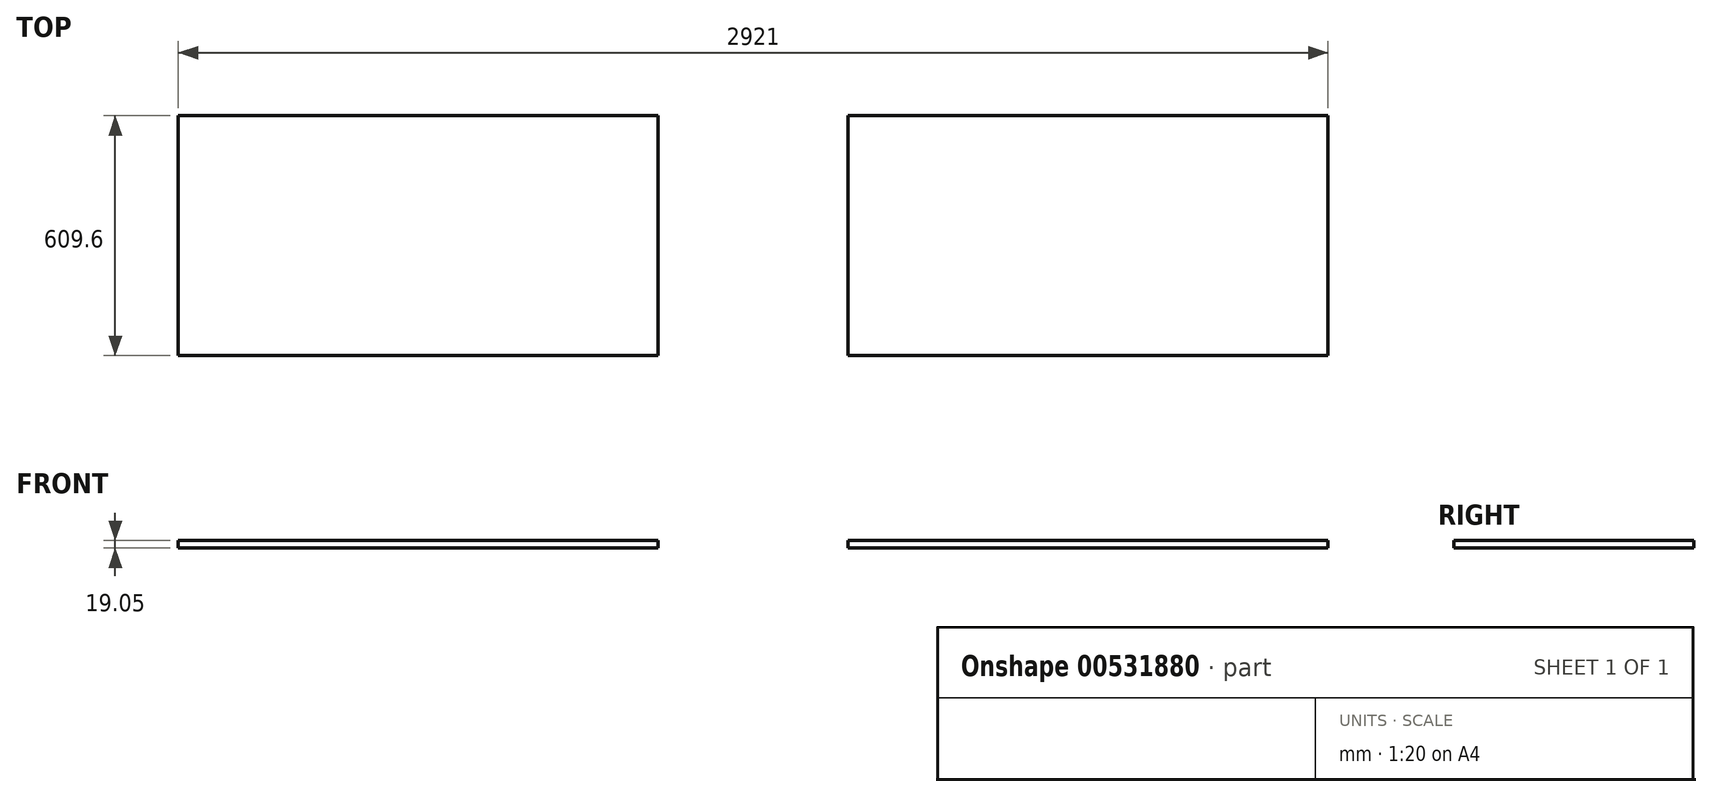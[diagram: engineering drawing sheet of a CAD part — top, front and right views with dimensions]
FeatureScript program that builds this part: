
annotation { "Feature Type Name" : "Feature", "Feature Type Description" : "" }
export const myFeature = defineFeature(function(context is Context, id is Id, definition is map)
    precondition{}
    {
        {
            var Q0;
            Q0=qCreatedBy(makeId("Top.planeOp"),FACE);
            var sketch = newSketch(context, id + "F0", { "sketchPlane" : qUnion([Q0])});
            skLineSegment(sketch, "E0.bottom", {"start": v(0, 0) * mm, "end": v(1219.2, 0) * mm});
            skLineSegment(sketch, "E0.top", {"start": v(0, 609.6) * mm, "end": v(1219.2, 609.6) * mm});
            skLineSegment(sketch, "E0.left", {"start": v(0, 0) * mm, "end": v(0, 609.6) * mm});
            skLineSegment(sketch, "E0.right", {"start": v(1219.2, 0) * mm, "end": v(1219.2, 609.6) * mm});
            skSolve(sketch);
        }
        {
            var Q0;
            Q0 = qSketchRegion(id + "F0", true);
            extrude(context, id + "F1", {"entities" : qUnion([Q0]), "depth" : 19.05 * mm, "offsetDistance" : 25.4 * mm});
        }
        {
            var Q0;
            Q0=makeQuery(id+"F1.opExtrude","CAP_FACE",FACE,{"disambiguationData":[OSD([sQuery(id+"F0.wireOp",EDGE,"E0.bottom"),sQuery(id+"F0.wireOp",EDGE,"E0.top"),sQuery(id+"F0.wireOp",EDGE,"E0.left"),sQuery(id+"F0.wireOp",EDGE,"E0.right")])],"isStart":false});
            var sketch = newSketch(context, id + "F2", { "sketchPlane" : qUnion([Q0])});
            skLineSegment(sketch, "E1.bottom", {"start": v(-1701.8, 609.6) * mm, "end": v(-482.6, 609.6) * mm});
            skLineSegment(sketch, "E1.top", {"start": v(-1701.8, 0) * mm, "end": v(-482.6, 0) * mm});
            skLineSegment(sketch, "E1.left", {"start": v(-1701.8, 609.6) * mm, "end": v(-1701.8, 0) * mm});
            skLineSegment(sketch, "E1.right", {"start": v(-482.6, 609.6) * mm, "end": v(-482.6, 0) * mm});
            skSolve(sketch);
        }
        {
            var Q0;
            Q0=makeQuery(id+"F2.imprint","IMPRINT",FACE,{"disambiguationData":[TD([[makeQuery(id+"F2.imprint","IMPRINT",EDGE,{"derivedFrom":sQuery(id+"F2.wireOp",EDGE,"E1.bottom")}),-1.0]])]});
            var Q1;
            Q1=makeQuery(id+"F1.opExtrude","CAP_FACE",FACE,{"disambiguationData":[OSD([sQuery(id+"F0.wireOp",EDGE,"E0.bottom"),sQuery(id+"F0.wireOp",EDGE,"E0.top"),sQuery(id+"F0.wireOp",EDGE,"E0.left"),sQuery(id+"F0.wireOp",EDGE,"E0.right")])],"isStart":false});
            var Q2;
            Q2=makeQuery(id+"F1.opExtrude","SWEPT_BODY",BODY,{"disambiguationData":[OSD([sQuery(id+"F0.wireOp",EDGE,"E0.bottom"),sQuery(id+"F0.wireOp",EDGE,"E0.top"),sQuery(id+"F0.wireOp",EDGE,"E0.left"),sQuery(id+"F0.wireOp",EDGE,"E0.right")])]});
            var Q3;
            Q3=makeQuery(id+"F1.opExtrude","CAP_VERTEX",VERTEX,{"disambiguationData":[OSD([sQuery(id+"F0.wireOp",EDGE,"E0.top"),sQuery(id+"F0.wireOp",EDGE,"E0.left")])],"isStart":false});
            extrude(context, id + "F3", {"entities" : qUnion([Q0]), "oppositeDirection" : true, "depth" : 19.05 * mm, "endBoundEntityFace" : qUnion([Q1]), "endBoundEntityBody" : qUnion([Q2]), "endBoundEntityVertex" : qUnion([Q3]), "offsetDistance" : 25.4 * mm});
        }
    });
